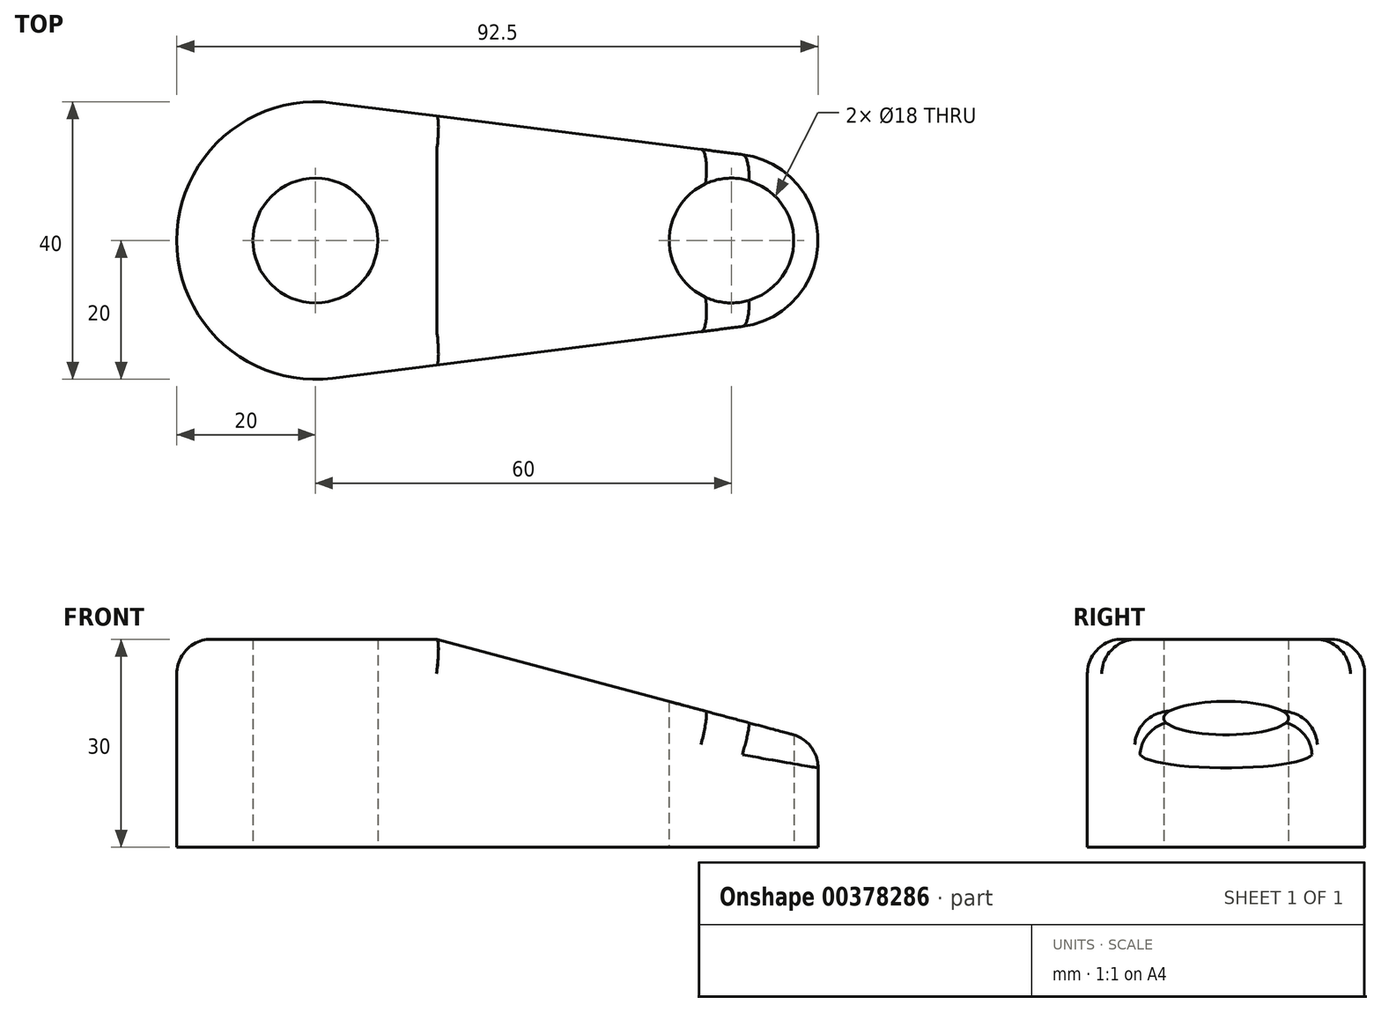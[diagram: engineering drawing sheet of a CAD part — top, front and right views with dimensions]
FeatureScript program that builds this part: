
annotation { "Feature Type Name" : "Feature", "Feature Type Description" : "" }
export const myFeature = defineFeature(function(context is Context, id is Id, definition is map)
    precondition{}
    {
        {
            var Q0;
            Q0=qCreatedBy(makeId("Top.planeOp"),FACE);
            var sketch = newSketch(context, id + "F0", { "sketchPlane" : qUnion([Q0])});
            skCircle(sketch, "E0", {"center": v(-60, 0) * mm, "radius": 20 * mm});
            skCircle(sketch, "E1", {"center": v(0, 0) * mm, "radius": 12.5 * mm});
            skLineSegment(sketch, "E2", {"start": v(1.56, 12.4) * mm, "end": v(-57.5, 19.84) * mm});
            skLineSegment(sketch, "E3", {"start": v(-57.5, -19.84) * mm, "end": v(1.56, -12.4) * mm});
            skCircle(sketch, "E4", {"center": v(-60, 0) * mm, "radius": 9 * mm});
            skCircle(sketch, "E5", {"center": v(0, 0) * mm, "radius": 9 * mm});
            skSolve(sketch);
        }
        {
            var Q0;
            Q0 = qSketchRegion(id + "F0", true);
            extrude(context, id + "F1", {"entities" : qUnion([Q0]), "depth" : 30 * mm});
        }
        {
            var Q0;
            Q0=qCreatedBy(makeId("Front.planeOp"),FACE);
            var sketch = newSketch(context, id + "F2", { "sketchPlane" : qUnion([Q0])});
            skLineSegment(sketch, "E6", {"start": v(-42.5, 30) * mm, "end": v(12.5, 15.26) * mm});
            skLineSegment(sketch, "E7", {"start": v(12.5, 15.26) * mm, "end": v(12.5, 30) * mm});
            skLineSegment(sketch, "E8.0", {"start": v(-57.5, 30) * mm, "end": v(1.56, 30) * mm});
            skLineSegment(sketch, "E9.0", {"start": v(1.56, 30) * mm, "end": v(12.5, 30) * mm});
            skSolve(sketch);
        }
        {
            var Q0;
            Q0 = qSketchRegion(id + "F2", true);
            extrude(context, id + "F3", {"entities" : qUnion([Q0]), "operationType" : NewBodyOperationType.REMOVE, "endBound" : BoundingType.SYMMETRIC, "depth" : 40 * mm});
        }
        {
            var Q0;
            Q0=makeQuery(id+"F3.boolean.opBoolean","INTERSECT",EDGE,{"derivedFrom":[makeQuery(id+"F1.opExtrude","SWEPT_FACE",FACE,{"disambiguationData":[OSD([sQuery(id+"F0.wireOp",EDGE,"E3")])]}),makeQuery(id+"F3.opExtrude","SWEPT_FACE",FACE,{"disambiguationData":[OSD([sQuery(id+"F2.wireOp",EDGE,"E6")])]})]});
            var Q1;
            Q1=makeQuery(id+"F1.opExtrude","CAP_EDGE",EDGE,{"disambiguationData":[OSD([sQuery(id+"F0.wireOp",EDGE,"E3")])],"isStart":false});
            fillet(context, id + "F4", {"entities" : qUnion([Q0, Q1]), "radius" : 5 * mm, "tangentPropagation" : true, "allowEdgeOverflow" : false});
        }
    });
